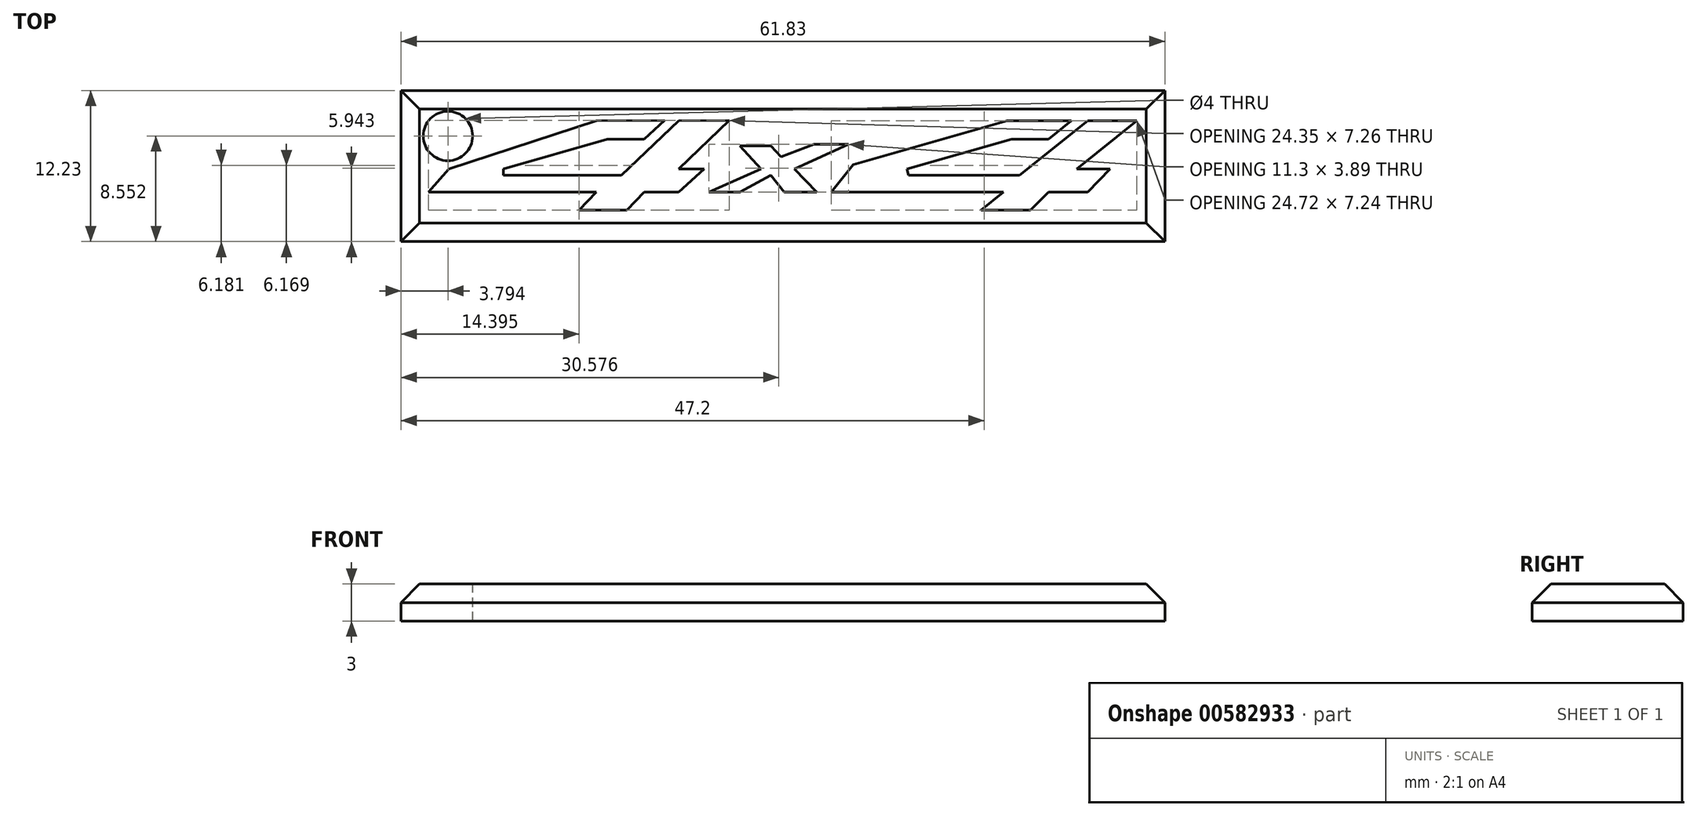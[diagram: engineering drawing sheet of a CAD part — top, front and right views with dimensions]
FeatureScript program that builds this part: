
annotation { "Feature Type Name" : "Feature", "Feature Type Description" : "" }
export const myFeature = defineFeature(function(context is Context, id is Id, definition is map)
    precondition{}
    {
        {
            var Q0;
            Q0=qCreatedBy(makeId("Top.planeOp"),FACE);
            var sketch = newSketch(context, id + "F0", { "sketchPlane" : qUnion([Q0])});
            skLineSegment(sketch, "E0", {"start": v(5.84, 0.87) * mm, "end": v(18.29, 4.43) * mm});
            skLineSegment(sketch, "E1", {"start": v(18.29, 4.43) * mm, "end": v(23.5, 4.43) * mm});
            skLineSegment(sketch, "E2", {"start": v(23.5, 4.43) * mm, "end": v(21.67, 2.95) * mm});
            skLineSegment(sketch, "E3", {"start": v(21.67, 2.95) * mm, "end": v(18.68, 2.95) * mm});
            skLineSegment(sketch, "E4", {"start": v(18.68, 2.95) * mm, "end": v(10.19, 0.52) * mm});
            skLineSegment(sketch, "E5", {"start": v(10.19, 0.52) * mm, "end": v(10.34, 0) * mm});
            skLineSegment(sketch, "E6", {"start": v(10.34, 0) * mm, "end": v(19.31, 0) * mm});
            skLineSegment(sketch, "E7", {"start": v(19.31, 0) * mm, "end": v(24.82, 4.43) * mm});
            skLineSegment(sketch, "E8", {"start": v(24.82, 4.43) * mm, "end": v(28.81, 4.43) * mm});
            skLineSegment(sketch, "E9", {"start": v(28.81, 4.43) * mm, "end": v(23.95, 0.52) * mm});
            skLineSegment(sketch, "E10", {"start": v(23.95, 0.52) * mm, "end": v(26.64, 0.52) * mm});
            skLineSegment(sketch, "E11", {"start": v(26.64, 0.52) * mm, "end": v(24.82, -1.36) * mm});
            skLineSegment(sketch, "E12", {"start": v(24.82, -1.36) * mm, "end": v(21.67, -1.36) * mm});
            skLineSegment(sketch, "E13", {"start": v(21.67, -1.36) * mm, "end": v(20.22, -2.8) * mm});
            skLineSegment(sketch, "E14", {"start": v(20.22, -2.8) * mm, "end": v(16.2, -2.8) * mm});
            skLineSegment(sketch, "E15", {"start": v(16.2, -2.8) * mm, "end": v(18.01, -1.36) * mm});
            skLineSegment(sketch, "E16", {"start": v(18.01, -1.36) * mm, "end": v(4.09, -1.36) * mm});
            skLineSegment(sketch, "E17", {"start": v(4.09, -1.36) * mm, "end": v(5.84, 0.87) * mm});
            skLineSegment(sketch, "E18", {"start": v(2.67, 2.53) * mm, "end": v(5.48, 2.53) * mm});
            skLineSegment(sketch, "E19", {"start": v(5.48, 2.53) * mm, "end": v(1.07, 0.54) * mm});
            skLineSegment(sketch, "E20", {"start": v(1.07, 0.54) * mm, "end": v(2.88, -1.36) * mm});
            skLineSegment(sketch, "E21", {"start": v(2.88, -1.36) * mm, "end": v(0.26, -1.36) * mm});
            skLineSegment(sketch, "E22", {"start": v(0.26, -1.36) * mm, "end": v(-0.83, 0) * mm});
            skLineSegment(sketch, "E23", {"start": v(-0.83, 0) * mm, "end": v(-3.33, -1.36) * mm});
            skLineSegment(sketch, "E24", {"start": v(-3.33, -1.36) * mm, "end": v(-5.82, -1.36) * mm});
            skLineSegment(sketch, "E25", {"start": v(-5.82, -1.36) * mm, "end": v(-1.62, 0.54) * mm});
            skLineSegment(sketch, "E26", {"start": v(-1.62, 0.54) * mm, "end": v(-3.33, 2.4) * mm});
            skLineSegment(sketch, "E27", {"start": v(-3.33, 2.4) * mm, "end": v(-0.83, 2.4) * mm});
            skLineSegment(sketch, "E28", {"start": v(-0.83, 2.4) * mm, "end": v(0, 1.5) * mm});
            skLineSegment(sketch, "E29", {"start": v(0, 1.5) * mm, "end": v(2.67, 2.53) * mm});
            skLineSegment(sketch, "E30", {"start": v(-4.18, 4.45) * mm, "end": v(-8.29, 0.54) * mm});
            skLineSegment(sketch, "E31", {"start": v(-8.29, 0.54) * mm, "end": v(-6.22, 0.54) * mm});
            skLineSegment(sketch, "E32", {"start": v(-6.22, 0.54) * mm, "end": v(-8.29, -1.36) * mm});
            skLineSegment(sketch, "E33", {"start": v(-8.29, -1.36) * mm, "end": v(-11.06, -1.36) * mm});
            skLineSegment(sketch, "E34", {"start": v(-11.06, -1.36) * mm, "end": v(-12.46, -2.8) * mm});
            skLineSegment(sketch, "E35", {"start": v(-12.46, -2.8) * mm, "end": v(-16.35, -2.8) * mm});
            skLineSegment(sketch, "E36", {"start": v(-16.35, -2.8) * mm, "end": v(-14.96, -1.36) * mm});
            skLineSegment(sketch, "E37", {"start": v(-14.96, -1.36) * mm, "end": v(-28.53, -1.36) * mm});
            skLineSegment(sketch, "E38", {"start": v(-28.53, -1.36) * mm, "end": v(-26.88, 0.54) * mm});
            skLineSegment(sketch, "E39", {"start": v(-26.88, 0.54) * mm, "end": v(-14.96, 4.43) * mm});
            skLineSegment(sketch, "E40", {"start": v(-14.96, 4.43) * mm, "end": v(-9.42, 4.45) * mm});
            skLineSegment(sketch, "E41", {"start": v(-9.42, 4.45) * mm, "end": v(-11.06, 2.94) * mm});
            skLineSegment(sketch, "E42", {"start": v(-11.06, 2.94) * mm, "end": v(-14.06, 2.94) * mm});
            skLineSegment(sketch, "E43", {"start": v(-14.06, 2.94) * mm, "end": v(-22.46, 0.54) * mm});
            skLineSegment(sketch, "E44", {"start": v(-22.46, 0.54) * mm, "end": v(-22.46, 0) * mm});
            skLineSegment(sketch, "E45", {"start": v(-22.46, 0) * mm, "end": v(-12.91, 0) * mm});
            skLineSegment(sketch, "E46", {"start": v(-12.91, 0) * mm, "end": v(-8.26, 4.43) * mm});
            skLineSegment(sketch, "E47", {"start": v(-8.26, 4.43) * mm, "end": v(-4.18, 4.45) * mm});
            skLineSegment(sketch, "E48.bottom", {"start": v(-30.75, 6.87) * mm, "end": v(31.08, 6.87) * mm});
            skLineSegment(sketch, "E48.top", {"start": v(-30.75, -5.36) * mm, "end": v(31.08, -5.36) * mm});
            skLineSegment(sketch, "E48.left", {"start": v(-30.75, 6.87) * mm, "end": v(-30.75, -5.36) * mm});
            skLineSegment(sketch, "E48.right", {"start": v(31.08, 6.87) * mm, "end": v(31.08, -5.36) * mm});
            skSolve(sketch);
        }
        {
            var Q0;
            Q0=makeQuery(id+"F0.imprint","IMPRINT",FACE,{"disambiguationData":[TD([[makeQuery(id+"F0.imprint","IMPRINT",EDGE,{"derivedFrom":sQuery(id+"F0.wireOp",EDGE,"E0")}),1.0]])]});
            extrude(context, id + "F1", {"entities" : qUnion([Q0]), "oppositeDirection" : true, "depth" : 3 * mm, "offsetDistance" : 25 * mm});
        }
        {
            var Q0;
            Q0=makeQuery(id+"F1.opExtrude","CAP_EDGE",EDGE,{"disambiguationData":[OSD([sQuery(id+"F0.wireOp",EDGE,"E48.bottom")])],"isStart":true});
            var Q1;
            Q1=makeQuery(id+"F1.opExtrude","CAP_EDGE",EDGE,{"disambiguationData":[OSD([sQuery(id+"F0.wireOp",EDGE,"E48.left")])],"isStart":true});
            var Q2;
            Q2=makeQuery(id+"F1.opExtrude","CAP_EDGE",EDGE,{"disambiguationData":[OSD([sQuery(id+"F0.wireOp",EDGE,"E48.top")])],"isStart":true});
            var Q3;
            Q3=makeQuery(id+"F1.opExtrude","CAP_EDGE",EDGE,{"disambiguationData":[OSD([sQuery(id+"F0.wireOp",EDGE,"E48.right")])],"isStart":true});
            chamfer(context, id + "F2", {"entities" : qUnion([Q0, Q1, Q2, Q3]), "width" : 1.5 * mm, "tangentPropagation" : true});
        }
        {
            var Q0;
            Q0=makeQuery(id+"F1.opExtrude","CAP_FACE",FACE,{"disambiguationData":[OSD([sQuery(id+"F0.wireOp",EDGE,"E0"),sQuery(id+"F0.wireOp",EDGE,"E1"),sQuery(id+"F0.wireOp",EDGE,"E2"),sQuery(id+"F0.wireOp",EDGE,"E3"),sQuery(id+"F0.wireOp",EDGE,"E4"),sQuery(id+"F0.wireOp",EDGE,"E5"),sQuery(id+"F0.wireOp",EDGE,"E6"),sQuery(id+"F0.wireOp",EDGE,"E7"),sQuery(id+"F0.wireOp",EDGE,"E8"),sQuery(id+"F0.wireOp",EDGE,"E9"),sQuery(id+"F0.wireOp",EDGE,"E10"),sQuery(id+"F0.wireOp",EDGE,"E11"),sQuery(id+"F0.wireOp",EDGE,"E12"),sQuery(id+"F0.wireOp",EDGE,"E13"),sQuery(id+"F0.wireOp",EDGE,"E14"),sQuery(id+"F0.wireOp",EDGE,"E15"),sQuery(id+"F0.wireOp",EDGE,"E16"),sQuery(id+"F0.wireOp",EDGE,"E17"),sQuery(id+"F0.wireOp",EDGE,"E18"),sQuery(id+"F0.wireOp",EDGE,"E19"),sQuery(id+"F0.wireOp",EDGE,"E20"),sQuery(id+"F0.wireOp",EDGE,"E21"),sQuery(id+"F0.wireOp",EDGE,"E22"),sQuery(id+"F0.wireOp",EDGE,"E23"),sQuery(id+"F0.wireOp",EDGE,"E24"),sQuery(id+"F0.wireOp",EDGE,"E25"),sQuery(id+"F0.wireOp",EDGE,"E26"),sQuery(id+"F0.wireOp",EDGE,"E27"),sQuery(id+"F0.wireOp",EDGE,"E28"),sQuery(id+"F0.wireOp",EDGE,"E29"),sQuery(id+"F0.wireOp",EDGE,"E30"),sQuery(id+"F0.wireOp",EDGE,"E31"),sQuery(id+"F0.wireOp",EDGE,"E32"),sQuery(id+"F0.wireOp",EDGE,"E33"),sQuery(id+"F0.wireOp",EDGE,"E34"),sQuery(id+"F0.wireOp",EDGE,"E35"),sQuery(id+"F0.wireOp",EDGE,"E36"),sQuery(id+"F0.wireOp",EDGE,"E37"),sQuery(id+"F0.wireOp",EDGE,"E38"),sQuery(id+"F0.wireOp",EDGE,"E39"),sQuery(id+"F0.wireOp",EDGE,"E40"),sQuery(id+"F0.wireOp",EDGE,"E41"),sQuery(id+"F0.wireOp",EDGE,"E42"),sQuery(id+"F0.wireOp",EDGE,"E43"),sQuery(id+"F0.wireOp",EDGE,"E44"),sQuery(id+"F0.wireOp",EDGE,"E45"),sQuery(id+"F0.wireOp",EDGE,"E46"),sQuery(id+"F0.wireOp",EDGE,"E47"),sQuery(id+"F0.wireOp",EDGE,"E48.bottom"),sQuery(id+"F0.wireOp",EDGE,"E48.top"),sQuery(id+"F0.wireOp",EDGE,"E48.left"),sQuery(id+"F0.wireOp",EDGE,"E48.right")])],"isStart":true});
            var sketch = newSketch(context, id + "F3", { "sketchPlane" : qUnion([Q0])});
            skCircle(sketch, "E49", {"center": v(-26.96, 3.2) * mm, "radius": 2 * mm});
            skSolve(sketch);
        }
        {
            var Q0;
            Q0=makeQuery(id+"F3.imprint","IMPRINT",FACE,{"disambiguationData":[TD([[makeQuery(id+"F3.imprint","IMPRINT",EDGE,{"derivedFrom":sQuery(id+"F3.wireOp",EDGE,"E49")}),1.0]])]});
            extrude(context, id + "F4", {"entities" : qUnion([Q0]), "operationType" : NewBodyOperationType.REMOVE, "oppositeDirection" : true, "depth" : 25 * mm, "offsetDistance" : 25 * mm});
        }
    });
